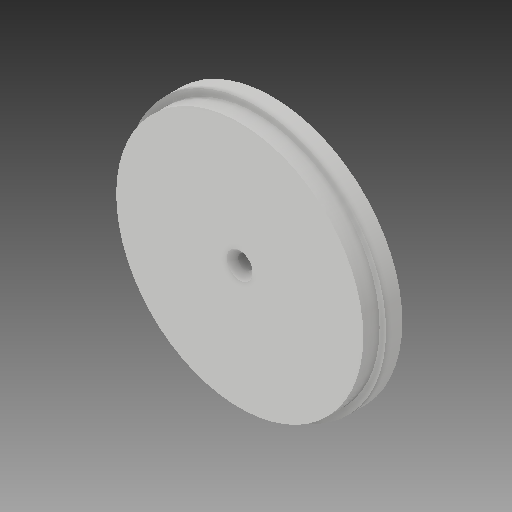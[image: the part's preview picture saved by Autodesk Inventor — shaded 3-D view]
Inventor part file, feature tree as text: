
AUTODESK INVENTOR PART (.ipt)
format: ipt  version: 2019 (Build 230136000, 136)  size: 127,488 bytes
history: native  units: mm
features: sketch x4, extrude x3, projected_geometry x2, other x1, hole x1
ambient origin geometry x8: Origin, YZ Plane, XZ Plane, XY Plane, X Axis, Y Axis, Z Axis, Center Point
bodies: Body1 (feature_tree)
feature tree (11):
  other  "Твердое тело1"
  extrude  "Выдавливание1"  Depth=80.0mm
  extrude  "Выдавливание2"  Depth=5.0mm TaperAngle=0.0deg
  extrude  "Выдавливание3"  Depth=4.0mm TaperAngle=0.0deg
  hole  "Отверстие1"  [1 undecoded]
  sketch  "Эскиз1"
  sketch  "Эскиз2"
  sketch  "Эскиз3"
  projected_geometry  "Спроецированная петля1"
  sketch  "Эскиз5"
  projected_geometry  "Спроецированная петля2"
note: 1 required parameter value undecoded (feature->parameter linkage not recoverable at this tier; creation-order binding heuristic only, values carry confidence <= 0.55)
